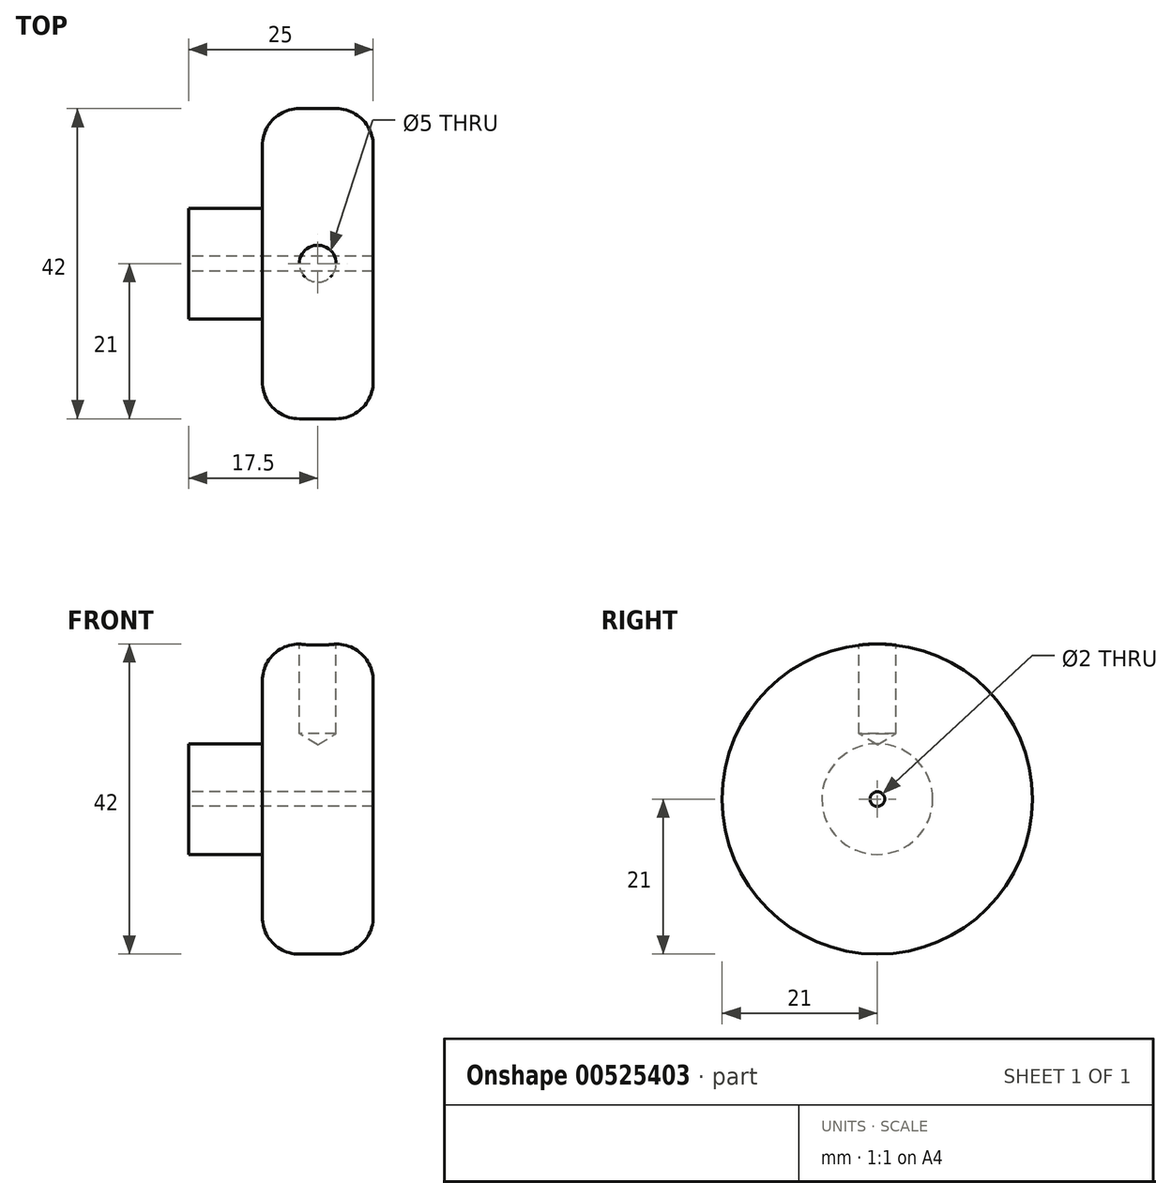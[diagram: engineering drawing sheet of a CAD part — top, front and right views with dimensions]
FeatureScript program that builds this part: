
annotation { "Feature Type Name" : "Feature", "Feature Type Description" : "" }
export const myFeature = defineFeature(function(context is Context, id is Id, definition is map)
    precondition{}
    {
        {
            var Q0;
            Q0=qCreatedBy(makeId("Front.planeOp"),FACE);
            var sketch = newSketch(context, id + "F0", { "sketchPlane" : qUnion([Q0])});
            skLineSegment(sketch, "E0", {"start": v(0, 1) * mm, "end": v(25, 1) * mm});
            skLineSegment(sketch, "E1", {"start": v(25, 1) * mm, "end": v(25, 21) * mm});
            skLineSegment(sketch, "E2", {"start": v(25, 21) * mm, "end": v(10, 21) * mm});
            skLineSegment(sketch, "E3", {"start": v(10, 21) * mm, "end": v(10, 7.5) * mm});
            skLineSegment(sketch, "E4", {"start": v(10, 7.5) * mm, "end": v(0, 7.5) * mm});
            skLineSegment(sketch, "E5", {"start": v(0, 7.5) * mm, "end": v(0, 1) * mm});
            skLineSegment(sketch, "E6", {"start": v(-47.95, 0) * mm, "end": v(74.35, 0) * mm});
            skSolve(sketch);
        }
        {
            var Q0;
            Q0=makeQuery(id+"F0.imprint","IMPRINT",FACE,{"disambiguationData":[TD([[makeQuery(id+"F0.imprint","IMPRINT",EDGE,{"derivedFrom":sQuery(id+"F0.wireOp",EDGE,"E0")}),1.0]])]});
            var Q1;
            Q1=sQuery(id+"F0.wireOp",EDGE,"E6");
            revolve(context, id + "F1", {"entities" : qUnion([Q0]), "axis" : qUnion([Q1]), "revolveType" : RevolveType.FULL});
        }
        {
            var Q0;
            Q0=makeQuery(id+"F1.opRevolve","SWEPT_EDGE",EDGE,{"disambiguationData":[OSD([sQuery(id+"F0.wireOp",EDGE,"E1"),sQuery(id+"F0.wireOp",EDGE,"E2")])]});
            var Q1;
            Q1=makeQuery(id+"F1.opRevolve","SWEPT_EDGE",EDGE,{"disambiguationData":[OSD([sQuery(id+"F0.wireOp",EDGE,"E2"),sQuery(id+"F0.wireOp",EDGE,"E3")])]});
            fillet(context, id + "F2", {"entities" : qUnion([Q0, Q1]), "radius" : 5 * mm, "tangentPropagation" : true, "allowEdgeOverflow" : false});
        }
        {
            var Q0;
            Q0=qCreatedBy(makeId("Top.planeOp"),FACE);
            cPlane(context, id + "F3", {"entities" : qUnion([Q0]), "cplaneType" : CPlaneType.OFFSET, "offset" : 21.4 * mm, "width" : 150 * mm, "height" : 150 * mm});
        }
        {
            var Q0;
            Q0=qCreatedBy(id+"F3.planeOp",FACE);
            var sketch = newSketch(context, id + "F4", { "sketchPlane" : qUnion([Q0])});
            skCircle(sketch, "E7", {"center": v(17.5, 0) * mm, "radius": 2.5 * mm});
            skSolve(sketch);
        }
        {
            var Q0;
            Q0=sQuery(id+"F4.wireOp",VERTEX,"E7.center");
            var Q1;
            Q1=makeQuery(id+"F1.opRevolve","SWEPT_BODY",BODY,{"disambiguationData":[OSD([sQuery(id+"F0.wireOp",EDGE,"E0"),sQuery(id+"F0.wireOp",EDGE,"E1"),sQuery(id+"F0.wireOp",EDGE,"E2"),sQuery(id+"F0.wireOp",EDGE,"E3"),sQuery(id+"F0.wireOp",EDGE,"E4"),sQuery(id+"F0.wireOp",EDGE,"E5")])]});
            hole(context, id + "F5", {"style" : HoleStyle.SIMPLE, "endStyle" : HoleEndStyle.BLIND, "holeDiameter" : 5 * mm, "holeDepth" : 12 * mm, "isTappedThrough" : true, "tappedDepth" : 12 * mm, "tapClearance" : 3, "locations" : qUnion([Q0]), "scope" : qUnion([Q1])});
        }
    });
